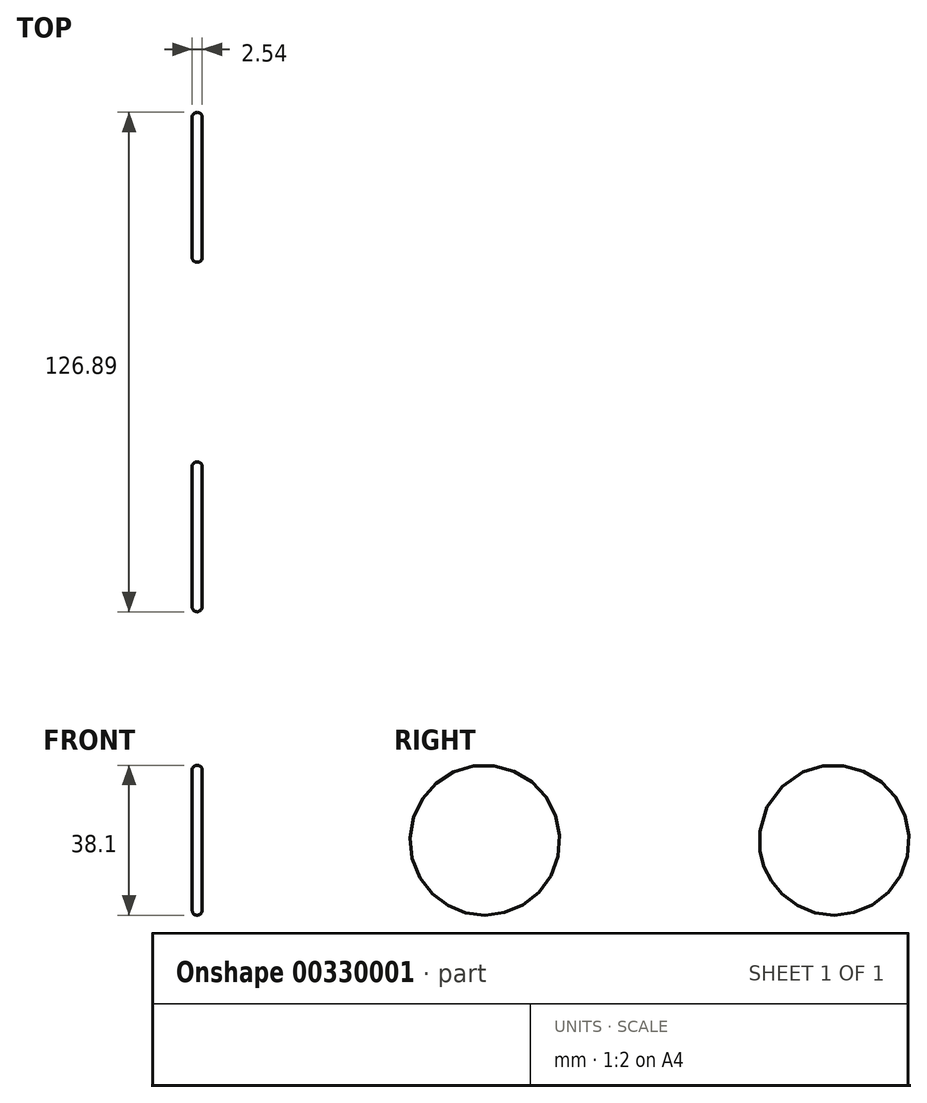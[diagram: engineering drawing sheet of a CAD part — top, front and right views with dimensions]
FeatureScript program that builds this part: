
annotation { "Feature Type Name" : "Feature", "Feature Type Description" : "" }
export const myFeature = defineFeature(function(context is Context, id is Id, definition is map)
    precondition{}
    {
        {
            var Q0;
            Q0=qCreatedBy(makeId("Right.planeOp"),FACE);
            var sketch = newSketch(context, id + "F0", { "sketchPlane" : qUnion([Q0])});
            skCircle(sketch, "E0", {"center": v(-88.79, 0) * mm, "radius": 19.05 * mm});
            skCircle(sketch, "E1", {"center": v(0, 0) * mm, "radius": 19.05 * mm});
            skSolve(sketch);
        }
        {
            var Q0;
            Q0 = qSketchRegion(id + "F0", true);
            extrude(context, id + "F1", {"entities" : qUnion([Q0]), "endBound" : BoundingType.SYMMETRIC, "depth" : 2.54 * mm});
        }
        {
            var Q0;
            Q0=makeQuery(id+"F1.opExtrude","CAP_EDGE",EDGE,{"disambiguationData":[OSD([sQuery(id+"F0.wireOp",EDGE,"E1")])],"isStart":false});
            var Q1;
            Q1=makeQuery(id+"F1.opExtrude","CAP_FACE",FACE,{"disambiguationData":[OSD([sQuery(id+"F0.wireOp",EDGE,"E1")])],"isStart":true});
            var Q2;
            Q2=makeQuery(id+"F1.opExtrude","CAP_EDGE",EDGE,{"disambiguationData":[OSD([sQuery(id+"F0.wireOp",EDGE,"E0")])],"isStart":false});
            var Q3;
            Q3=makeQuery(id+"F1.opExtrude","CAP_EDGE",EDGE,{"disambiguationData":[OSD([sQuery(id+"F0.wireOp",EDGE,"E0")])],"isStart":true});
            fillet(context, id + "F2", {"entities" : qUnion([Q0, Q1, Q2, Q3]), "radius" : 1.27 * mm, "tangentPropagation" : true, "allowEdgeOverflow" : false});
        }
    });
